# Revit family: 712-0220-001-DN100
name_source: partatom
category: Pipe Fittings
units: mm (PartAtom-declared; Revit-internal decimal feet)

## family parameters
Always vertical = Yes
Cut with Voids When Loaded = No
Part Type = Elbow
Round Connector Dimension = Use Diameter
Shared = No
Work Plane-Based = No

## types (1)
- DN100_PN10/16
    A = 22.50°
    Body_wallthickness = 115 mm
    DN 100_PN10/16 = 712-0100-02-201
    DN100_PN10/16 = Yes
    Description_ = AVK FLANGED BEND 22.5° W/LOOSE FLANGES
    FOD = 110 mm  [stored 0.360892 ft]
    Flange_thickness = 17 mm  [stored 0.0557743 ft]
    ID(Radius) = 50 mm  [stored 0.164042 ft]
    L = 110 mm  [stored 0.360892 ft]
    Nominal Diameter(DN) = 100 mm  [stored 0.328084 ft]
    URL product pages = https://www.avkvalves.com

note: [stored X ft] marks values corroborated as IEEE doubles in the binary element streams (Revit-internal decimal feet)

## geometry (parser evidence)
native form markers: Sweep x12
no freeform markers — native parametric forms only
